# Revit family: LRTB
name_source: partatom
category: Lighting Fixtures
units: mm (PartAtom-declared; Revit-internal decimal feet)

## family parameters
Always vertical = Yes
Cut with Voids When Loaded = No
Host = Ceiling
Light Source = Yes
OmniClass Number = 23.80.70.11.14.17
OmniClass Title = Direct/Indirect
Part Type = Normal
Room Calculation Point = No
Round Connector Dimension = Use Diameter
Shared = No

## types (4) — shared parameters
Assembly Code = D5020200
Color Filter = 16777215
Description = LED Troffer Dish Parallel Tear Drop
Dimming Lamp Color Temperature Shift = <None>
Emit Shape Visible in Rendering = No
Emit from Rectangle Width = 1' - 11 3/4"
Housing Finish = Metal - Viscor - White
Lamp = LED
Lens Finish = Acrylic - Viscor - Frosted Ribbed Linear Extruded
Manufacturer = VISIONEERING by VISCOR
Model = LRTB
Tilt Angle = 90.00°
URL = https://www.viscor.com
Voltage = 120 V
Width = 1' - 11 3/4"

## per-type parameters (varying)
| type | Apparent Load | Emit from Rectangle Length | Lamp Wattage | Length | Photometric Web File |
| LRTB2X2-LED840K020LUNV | 20 VA | 1' - 11 3/4" | 20 VA | 1' - 11 3/4" | LRTB2X2-LED840K020LUNV.ies |
| LRTB2x2-LED840K033LUNV | 26 VA | 1' - 11 3/4" | 26 VA | 1' - 11 3/4" | LRTB2x2-LED840K033LUNV.IES |
| LRTB2x4-LED840K046LUNV | 44 VA | 3' - 11 3/4" | 44 VA | 3' - 11 3/4" | LRTB2x4-LED840K046LUNV.IES |
| LRTB2x4-LED840K037LUNV | 28 VA | 3' - 11 3/4" | 28 VA | 3' - 11 3/4" | LRTB2X4-LED840K037LUNV.ies |

## geometry (parser evidence)
native form markers: Sweep x2
no freeform markers — native parametric forms only
